FCSTD DOCUMENT  (FreeCAD 0.18R4 (GitTag))
Label: spring
License: All rights reserved
LicenseURL: http://en.wikipedia.org/wiki/All_rights_reserved
objects: Sketcher::SketchObject×1
note: 1 computed .brp shape members not serialized (recipe doc carries the construction recipe); baked Part::Feature solids carry a one-line shape summary decoded from their .brp

FEATURE [Sketcher::SketchObject] Sketch
  sketch-geometry (7):
    g0: LineSegment [constr] StartX=3 StartY=3 StartZ=0 EndX=0 EndY=3 EndZ=0
    g1: LineSegment [constr] StartX=3 StartY=3 StartZ=0 EndX=3 EndY=0 EndZ=0
    g2: ArcOfCircle CenterX=3 CenterY=3 CenterZ=0 NormalX=0 NormalY=0 NormalZ=1 AngleXU=0 Radius=3 StartAngle=4.71239 EndAngle=9.42478
    g3: LineSegment [constr] StartX=3 StartY=0 StartZ=0 EndX=3 EndY=-3 EndZ=0
    g4: LineSegment [constr] StartX=0 StartY=3 StartZ=0 EndX=-3 EndY=3 EndZ=0
    g5: ArcOfCircle CenterX=3 CenterY=-1.5 CenterZ=0 NormalX=0 NormalY=0 NormalZ=1 AngleXU=0 Radius=1.5 StartAngle=1.5708 EndAngle=3.14159
    g6: ArcOfCircle CenterX=-1.5 CenterY=3 CenterZ=0 NormalX=0 NormalY=0 NormalZ=1 AngleXU=0 Radius=1.5 StartAngle=4.71239 EndAngle=6.28319
  constraints (22):
    c: Horizontal(g0)
    c: Coincident(g1,g0)
    c: PointOnObject(g1,g-1)
    c: Equal(g0,g1)
    c: Coincident(g2,g0)
    c: Coincident(g2,g0)
    c: Coincident(g2,g1)
    c: Coincident(g3,g2)
    c: Vertical(g3)
    c: Coincident(g4,g2)
    c: Horizontal(g4)
    c: Parallel(g3,g1)
    c: Equal(g4,g0)
    c: Coincident(g6,g2)
    c: Symmetric(g3,g3,g5)
    c: Symmetric(g4,g4,g6)
    c: Coincident(g5,g2)
    c: Angle(g5) = 1.5708
    c: Angle(g6) = 1.5708
    c: Equal(g3,g4)
    c: DistanceX(g0,g0) = 3
    c: DistanceX(g-1,g2) = 0
